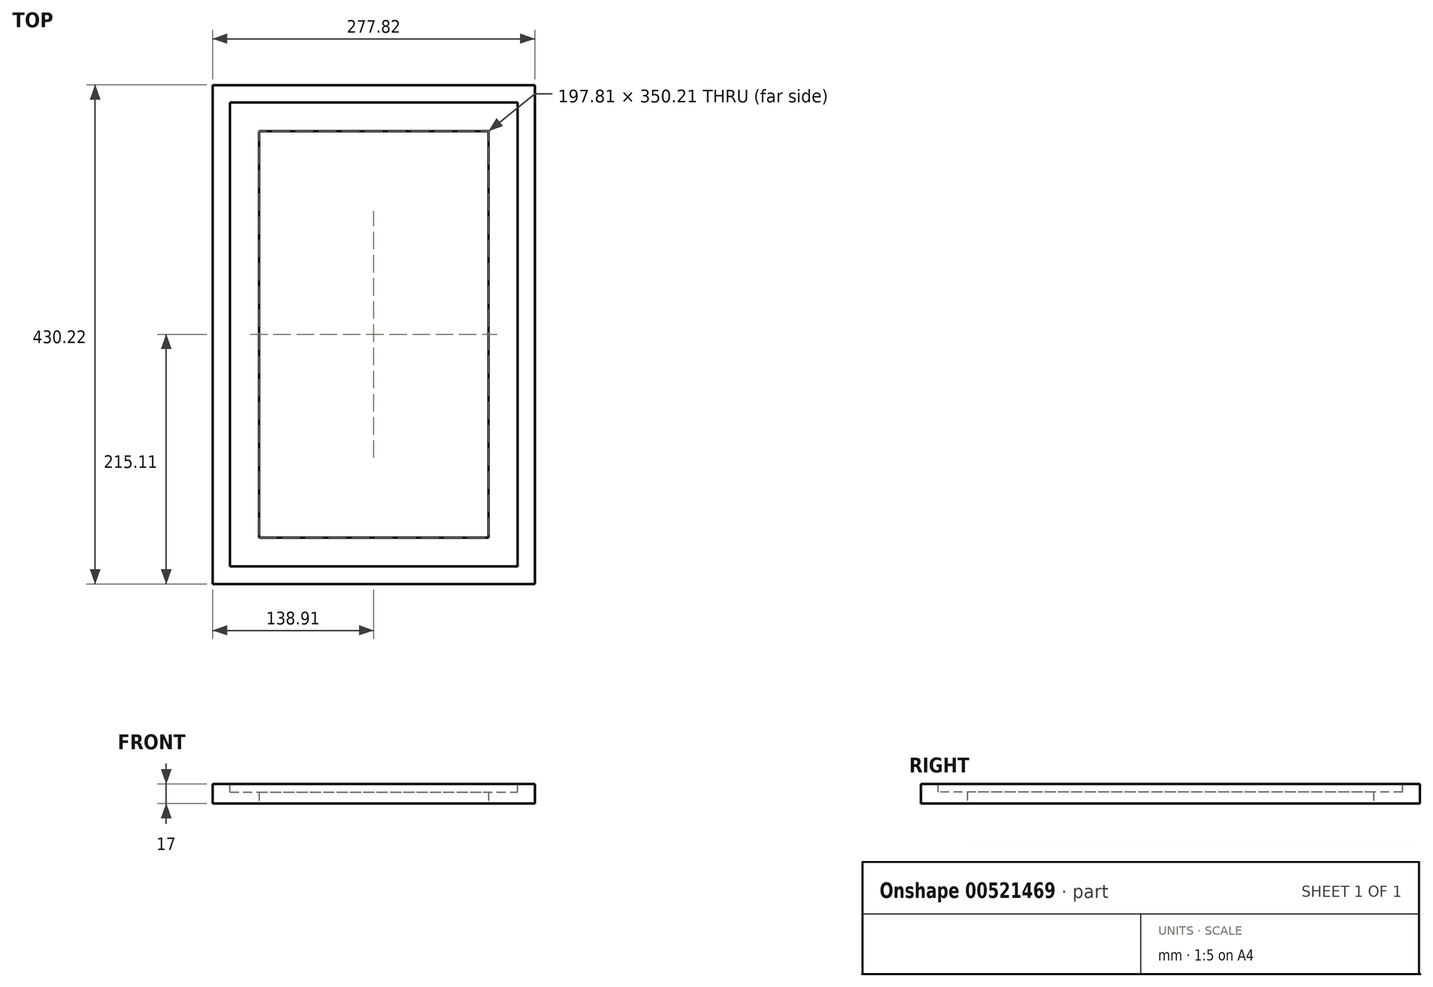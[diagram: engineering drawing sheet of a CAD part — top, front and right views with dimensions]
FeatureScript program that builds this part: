
annotation { "Feature Type Name" : "Feature", "Feature Type Description" : "" }
export const myFeature = defineFeature(function(context is Context, id is Id, definition is map)
    precondition{}
    {
        {
            var Q0;
            Q0=qCreatedBy(makeId("Top.planeOp"),FACE);
            var sketch = newSketch(context, id + "F0", { "sketchPlane" : qUnion([Q0])});
            skLineSegment(sketch, "E0.bottom", {"start": v(138.9, 215.1) * mm, "end": v(-138.9, 215.1) * mm});
            skLineSegment(sketch, "E0.top", {"start": v(138.9, -215.1) * mm, "end": v(-138.9, -215.1) * mm});
            skLineSegment(sketch, "E0.left", {"start": v(138.9, 215.1) * mm, "end": v(138.9, -215.1) * mm});
            skLineSegment(sketch, "E0.right", {"start": v(-138.9, 215.1) * mm, "end": v(-138.9, -215.1) * mm});
            skPoint(sketch, "E0.middle", {"position": v(0, 0) * mm});
            skLineSegment(sketch, "E1.bottom", {"start": v(-98.9, 175.1) * mm, "end": v(98.9, 175.1) * mm});
            skLineSegment(sketch, "E1.top", {"start": v(-98.9, -175.1) * mm, "end": v(98.9, -175.1) * mm});
            skLineSegment(sketch, "E1.left", {"start": v(-98.9, 175.1) * mm, "end": v(-98.9, -175.1) * mm});
            skLineSegment(sketch, "E1.right", {"start": v(98.9, 175.1) * mm, "end": v(98.9, -175.1) * mm});
            skSolve(sketch);
        }
        {
            var Q0;
            Q0=makeQuery(id+"F0.imprint","IMPRINT",FACE,{"disambiguationData":[TD([[makeQuery(id+"F0.imprint","IMPRINT",EDGE,{"derivedFrom":sQuery(id+"F0.wireOp",EDGE,"E0.bottom")}),1.0]])]});
            extrude(context, id + "F1", {"entities" : qUnion([Q0]), "depth" : 17 * mm, "offsetDistance" : 25 * mm});
        }
        {
            var Q0;
            Q0=makeQuery(id+"F1.opExtrude","CAP_FACE",FACE,{"disambiguationData":[OSD([sQuery(id+"F0.wireOp",EDGE,"E0.bottom"),sQuery(id+"F0.wireOp",EDGE,"E0.top"),sQuery(id+"F0.wireOp",EDGE,"E0.left"),sQuery(id+"F0.wireOp",EDGE,"E0.right"),sQuery(id+"F0.wireOp",EDGE,"E1.bottom"),sQuery(id+"F0.wireOp",EDGE,"E1.top"),sQuery(id+"F0.wireOp",EDGE,"E1.left"),sQuery(id+"F0.wireOp",EDGE,"E1.right")])],"isStart":false});
            var sketch = newSketch(context, id + "F2", { "sketchPlane" : qUnion([Q0])});
            skLineSegment(sketch, "E2.bottom", {"start": v(-123.9, 200.1) * mm, "end": v(123.9, 200.1) * mm});
            skLineSegment(sketch, "E2.top", {"start": v(-123.9, -200.1) * mm, "end": v(123.9, -200.1) * mm});
            skLineSegment(sketch, "E2.left", {"start": v(-123.9, 200.1) * mm, "end": v(-123.9, -200.1) * mm});
            skLineSegment(sketch, "E2.right", {"start": v(123.9, 200.1) * mm, "end": v(123.9, -200.1) * mm});
            skPoint(sketch, "E2.middle", {"position": v(0, 0) * mm});
            skSolve(sketch);
        }
        {
            var Q0;
            Q0=makeQuery(id+"F2.imprint","IMPRINT",FACE,{"disambiguationData":[TD([[makeQuery(id+"F2.imprint","IMPRINT",EDGE,{"derivedFrom":sQuery(id+"F2.wireOp",EDGE,"E2.bottom")}),-1.0]])]});
            extrude(context, id + "F3", {"entities" : qUnion([Q0]), "operationType" : NewBodyOperationType.REMOVE, "oppositeDirection" : true, "depth" : 7 * mm, "offsetDistance" : 25 * mm});
        }
    });
